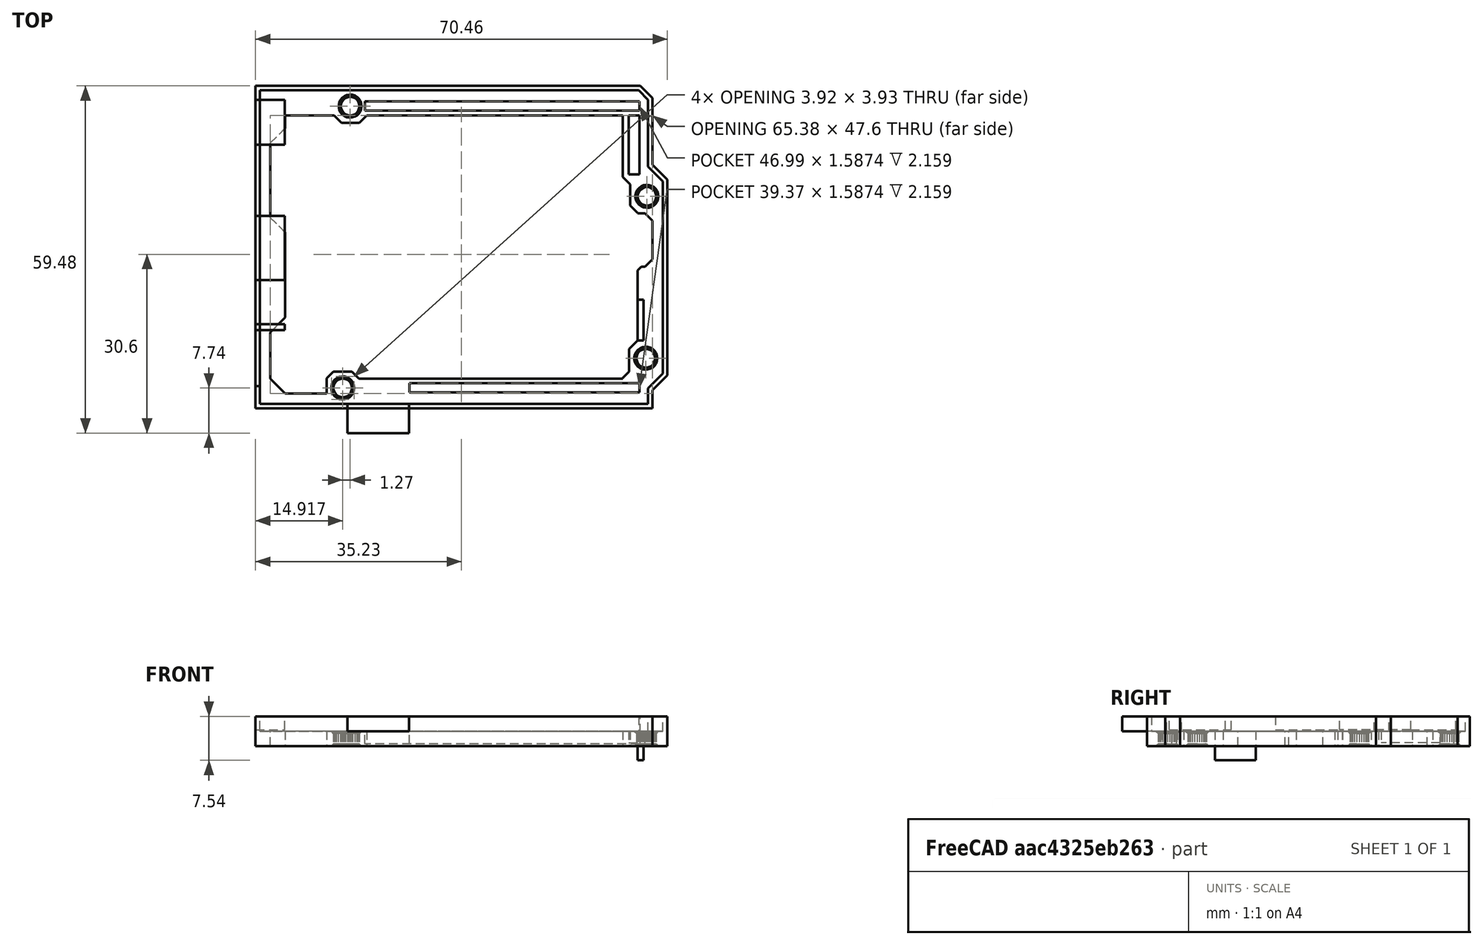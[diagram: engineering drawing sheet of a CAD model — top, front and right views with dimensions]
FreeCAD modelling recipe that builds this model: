
FCSTD DOCUMENT  (FreeCAD 0.16R6712 (Git))
Label: Soporte_BQ-Zum
License: CreativeCommons Attribution-ShareAlike
LicenseURL: http://creativecommons.org/licenses/by-sa/4.0/
objects: Sketcher::SketchObject×6, PartDesign::Pocket×6, Part::Feature×3, Mesh::Feature×1
note: 21 computed .brp shape members not serialized (recipe doc carries the construction recipe); baked Part::Feature solids carry a one-line shape summary decoded from their .brp

FEATURE [Mesh::Feature] Arduino_Bumper_0006
FEATURE [Part::Feature] Arduino_Bumper_0006001
  shape: bbox 70.46 x 55.22 x 5.08 mm, 1108 faces, 0 solids (baked)
FEATURE [Part::Feature] Arduino_Bumper_0006001_solid  label="Arduino_Bumper_0006001 (Solid)"
  shape: bbox 70.46 x 55.22 x 5.08 mm, 1108 faces (baked)
FEATURE [Part::Feature] Arduino_Bumper_0006001_solid001  label="Arduino_Bumper_0006001 (Solid)001"
  shape: bbox 70.46 x 55.22 x 5.08 mm, 577 faces (baked)
FEATURE [Sketcher::SketchObject] Sketch
  ExternalGeometry = -> [Arduino_Bumper_0006001_solid001]
  Placement = pos=(-35.2298,0,0) rot=(0.57735,-0.57735,-0.57735;2.0944rad)
  Support = -> Arduino_Bumper_0006001_solid001 [Face576]
  sketch-geometry (5):
    g0: LineSegment StartX=-17.526 StartY=2.794 StartZ=0 EndX=-25.2098 EndY=2.794 EndZ=0
    g1: LineSegment StartX=-25.2098 StartY=2.794 StartZ=0 EndX=-25.2098 EndY=5.08 EndZ=0
    g2: LineSegment StartX=-25.2098 StartY=5.08 StartZ=0 EndX=-17.526 EndY=5.08 EndZ=0
    g3: LineSegment StartX=-17.526 StartY=5.08 StartZ=0 EndX=-17.526 EndY=2.794 EndZ=0
    g4: GeomPoint [constr] X=-17.4588 Y=4.96498 Z=0
  constraints (11):
    c: Coincident(g0,g1)
    c: Coincident(g1,g2)
    c: Coincident(g2,g3)
    c: Coincident(g3,g0)
    c: Horizontal(g0)
    c: Horizontal(g2)
    c: Vertical(g1)
    c: Vertical(g3)
    c: Equal(g3,g-4)
    c: Coincident(g0,g-5)
    c: DistanceX(g-3,g1) = 2.4
FEATURE [PartDesign::Pocket] Pocket
  Length = 5
  Sketch = -> Sketch
  Type = 0
FEATURE [Sketcher::SketchObject] Sketch001
  ExternalGeometry = -> [Pocket]
  Placement = pos=(-35.2298,0,0) rot=(0.57735,-0.57735,-0.57735;2.0944rad)
  Support = -> Pocket [Face8]
  sketch-geometry (5):
    g0: LineSegment StartX=-5.334 StartY=5.08 StartZ=0 EndX=5.666 EndY=5.08 EndZ=0
    g1: LineSegment StartX=5.666 StartY=5.08 StartZ=0 EndX=5.666 EndY=2.794 EndZ=0
    g2: LineSegment StartX=5.666 StartY=2.794 StartZ=0 EndX=-5.334 EndY=2.794 EndZ=0
    g3: LineSegment StartX=-5.334 StartY=2.794 StartZ=0 EndX=-5.334 EndY=5.08 EndZ=0
    g4: GeomPoint [constr] X=-5.25993 Y=5.01849 Z=0
  constraints (11):
    c: Coincident(g0,g1)
    c: Coincident(g1,g2)
    c: Coincident(g2,g3)
    c: Coincident(g3,g0)
    c: Horizontal(g0)
    c: Horizontal(g2)
    c: Vertical(g1)
    c: Vertical(g3)
    c: Coincident(g0,g-3)
    c: Coincident(g2,g-3)
    c: DistanceX(g0,g0) = 11
FEATURE [PartDesign::Pocket] Pocket001
  Length = 5
  Sketch = -> Sketch001
  Type = 0
FEATURE [Sketcher::SketchObject] Sketch002
  ExternalGeometry = -> [Pocket001]
  Placement = pos=(-35.2298,0,0) rot=(0.57735,-0.57735,-0.57735;2.0944rad)
  Support = -> Pocket001 [Face8]
  sketch-geometry (4):
    g0: LineSegment StartX=13.224 StartY=5.08 StartZ=0 EndX=14.224 EndY=5.08 EndZ=0
    g1: LineSegment StartX=14.224 StartY=5.08 StartZ=0 EndX=14.224 EndY=2.794 EndZ=0
    g2: LineSegment StartX=14.224 StartY=2.794 StartZ=0 EndX=13.224 EndY=2.794 EndZ=0
    g3: LineSegment StartX=13.224 StartY=2.794 StartZ=0 EndX=13.224 EndY=5.08 EndZ=0
  constraints (11):
    c: Coincident(g0,g1)
    c: Coincident(g1,g2)
    c: Coincident(g2,g3)
    c: Coincident(g3,g0)
    c: Horizontal(g0)
    c: Horizontal(g2)
    c: Vertical(g1)
    c: Vertical(g3)
    c: Coincident(g0,g-3)
    c: Coincident(g1,g-3)
    c: DistanceX(g0,g0) = 1
FEATURE [PartDesign::Pocket] Pocket002
  Length = 5
  Sketch = -> Sketch002
  Type = 0
FEATURE [Sketcher::SketchObject] Sketch003
  ExternalGeometry = -> [Pocket002]
  Placement = pos=(0,-26.8732,0) rot=(0,0.707107,0.707107;3.14159rad)
  Support = -> Pocket002 [Face273]
  sketch-geometry (4):
    g0: LineSegment StartX=19.4932 StartY=5.08 StartZ=0 EndX=8.9932 EndY=5.08 EndZ=0
    g1: LineSegment StartX=8.9932 StartY=5.08 StartZ=0 EndX=8.9932 EndY=2.54 EndZ=0
    g2: LineSegment StartX=8.9932 StartY=2.54 StartZ=0 EndX=19.4932 EndY=2.54 EndZ=0
    g3: LineSegment StartX=19.4932 StartY=2.54 StartZ=0 EndX=19.4932 EndY=5.08 EndZ=0
  constraints (12):
    c: Coincident(g0,g1)
    c: Coincident(g1,g2)
    c: Coincident(g2,g3)
    c: Coincident(g3,g0)
    c: Horizontal(g0)
    c: Horizontal(g2)
    c: Vertical(g1)
    c: Vertical(g3)
    c: Equal(g3,g-3)
    c: PointOnObject(g2,g-4)
    c: DistanceX(g0,g-3) = 15
    c: DistanceX(g0,g0) = 10.5
FEATURE [PartDesign::Pocket] Pocket003
  Length = 5
  Sketch = -> Sketch003
  Type = 0
FEATURE [Sketcher::SketchObject] Sketch005
  ExternalGeometry = -> [Pocket003]
  Placement = pos=(0,0,2.54) rot=(0,0,1;0rad)
  Support = -> Pocket003 [Face571]
  sketch-geometry (4):
    g0: LineSegment StartX=30.1498 StartY=-9.002 StartZ=0 EndX=31.1498 EndY=-9.002 EndZ=0
    g1: LineSegment StartX=31.1498 StartY=-9.002 StartZ=0 EndX=31.1498 EndY=-16.002 EndZ=0
    g2: LineSegment StartX=31.1498 StartY=-16.002 StartZ=0 EndX=30.1498 EndY=-16.002 EndZ=0
    g3: LineSegment StartX=30.1498 StartY=-16.002 StartZ=0 EndX=30.1498 EndY=-9.002 EndZ=0
  constraints (12):
    c: Coincident(g0,g1)
    c: Coincident(g1,g2)
    c: Coincident(g2,g3)
    c: Coincident(g3,g0)
    c: Horizontal(g0)
    c: Horizontal(g2)
    c: Vertical(g1)
    c: Vertical(g3)
    c: PointOnObject(g0,g-3)
    c: DistanceY(g1,g1) = 7
    c: Coincident(g2,g-3)
    c: DistanceX(g0,g0) = 1
FEATURE [PartDesign::Pocket] Pocket004
  Length = 5
  Sketch = -> Sketch005
  Type = 0
FEATURE [Sketcher::SketchObject] Sketch006
  Placement = pos=(0,0,2.54) rot=(0,0,1;0rad)
  Support = -> Pocket004 [Face4]
  sketch-geometry (4):
    g0: LineSegment StartX=28.6384 StartY=22.5338 StartZ=0 EndX=30.4816 EndY=22.5338 EndZ=0
    g1: LineSegment StartX=30.4816 StartY=22.5338 StartZ=0 EndX=30.4816 EndY=12.4727 EndZ=0
    g2: LineSegment StartX=30.4816 StartY=12.4727 StartZ=0 EndX=28.6384 EndY=12.4727 EndZ=0
    g3: LineSegment StartX=28.6384 StartY=12.4727 StartZ=0 EndX=28.6384 EndY=22.5338 EndZ=0
  constraints (8):
    c: Coincident(g0,g1)
    c: Coincident(g1,g2)
    c: Coincident(g2,g3)
    c: Coincident(g3,g0)
    c: Horizontal(g0)
    c: Horizontal(g2)
    c: Vertical(g1)
    c: Vertical(g3)
FEATURE [PartDesign::Pocket] Pocket005
  Length = 2
  Sketch = -> Sketch006
  Type = 0
